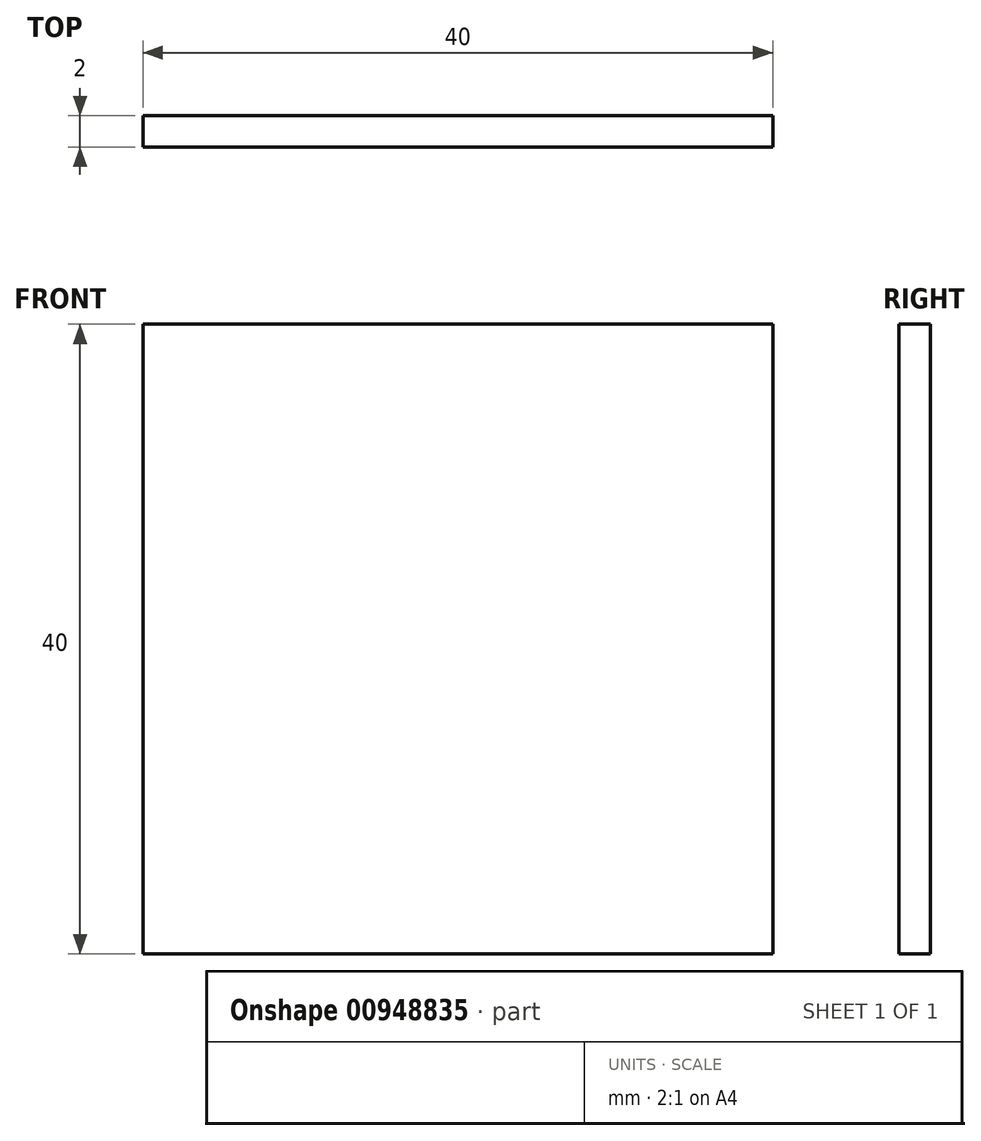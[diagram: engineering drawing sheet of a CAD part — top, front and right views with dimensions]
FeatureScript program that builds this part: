
annotation { "Feature Type Name" : "Feature", "Feature Type Description" : "" }
export const myFeature = defineFeature(function(context is Context, id is Id, definition is map)
    precondition{}
    {
        {
            var Q0;
            Q0=qCreatedBy(makeId("Front.planeOp"),FACE);
            var sketch = newSketch(context, id + "F0", { "sketchPlane" : qUnion([Q0])});
            skLineSegment(sketch, "E0.bottom", {"start": v(20, -20) * mm, "end": v(-20, -20) * mm});
            skLineSegment(sketch, "E0.top", {"start": v(20, 20) * mm, "end": v(-20, 20) * mm});
            skLineSegment(sketch, "E0.left", {"start": v(20, -20) * mm, "end": v(20, 20) * mm});
            skLineSegment(sketch, "E0.right", {"start": v(-20, -20) * mm, "end": v(-20, 20) * mm});
            skPoint(sketch, "E0.middle", {"position": v(0, 0) * mm});
            skSolve(sketch);
        }
        {
            var Q0;
            Q0=qSketchRegion(id+"F0",true);
            extrude(context, id + "F1", {"entities" : qUnion([Q0]), "depth" : 2 * mm, "offsetDistance" : 25 * mm});
        }
    });
